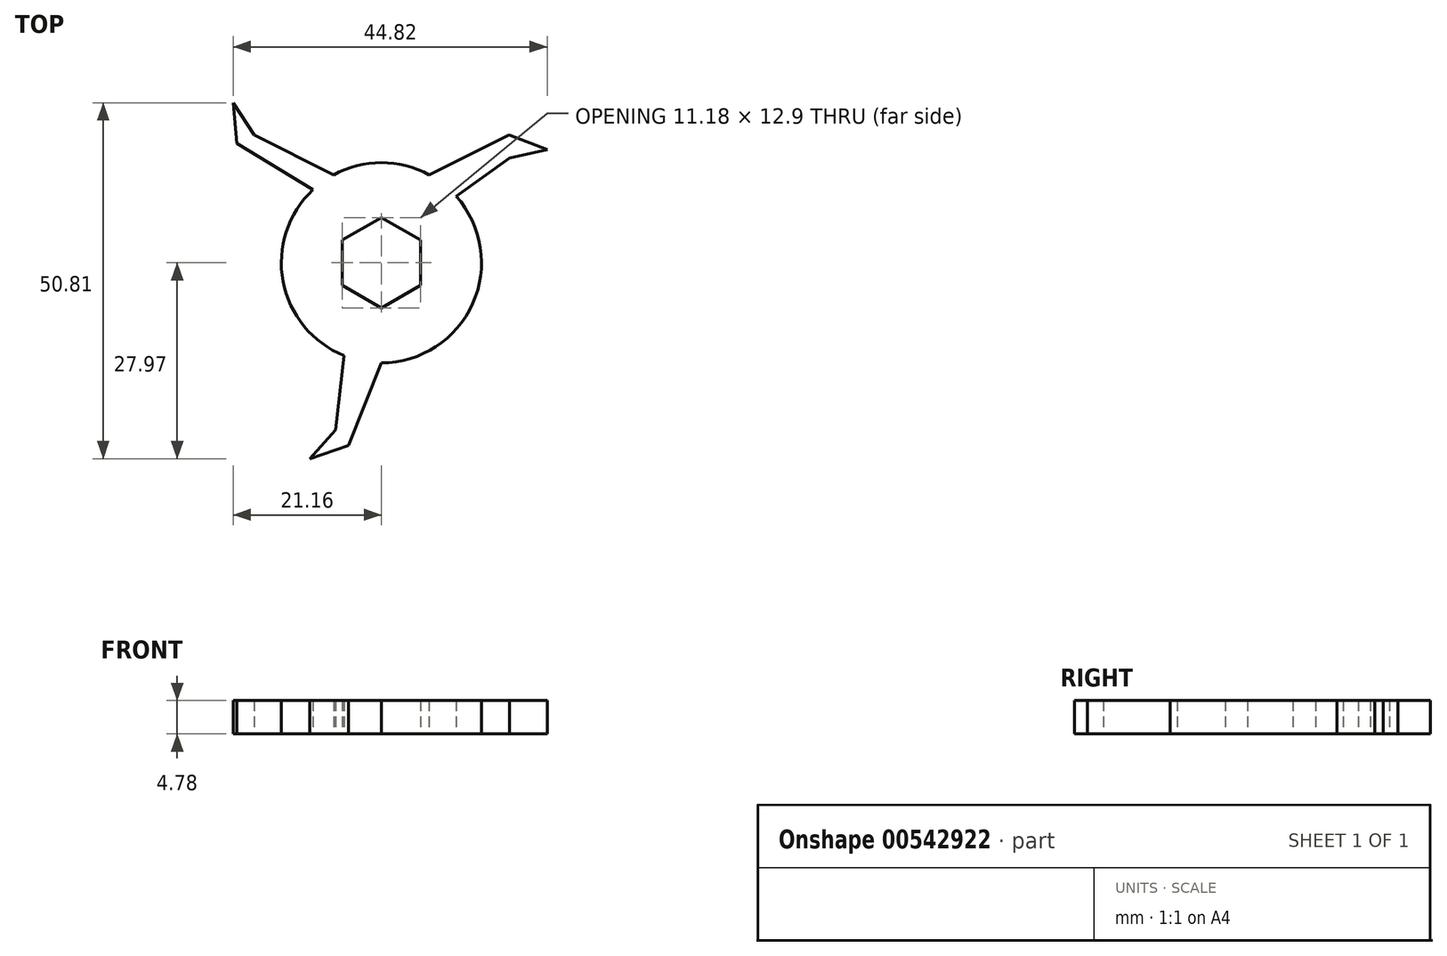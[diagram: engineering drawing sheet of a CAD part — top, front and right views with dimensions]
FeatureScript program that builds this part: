
annotation { "Feature Type Name" : "Feature", "Feature Type Description" : "" }
export const myFeature = defineFeature(function(context is Context, id is Id, definition is map)
    precondition{}
    {
        {
            var Q0;
            Q0=qCreatedBy(makeId("Top.planeOp"),FACE);
            var sketch = newSketch(context, id + "F0", { "sketchPlane" : qUnion([Q0])});
            skCircle(sketch, "E0", {"center": v(0, 0) * mm, "radius": 14.29 * mm});
            skPoint(sketch, "E1.end.orphan", {"position": v(12.7, 14.29) * mm});
            skPoint(sketch, "E1.start.orphan", {"position": v(0, 14.29) * mm});
            skPoint(sketch, "E2.start.orphan", {"position": v(13.26, 14.29) * mm});
            skPoint(sketch, "E3.start.orphan", {"position": v(12.7, 11.87) * mm});
            skPoint(sketch, "E4.end.orphan", {"position": v(-8.69, -11.34) * mm});
            skPoint(sketch, "E5.end.orphan", {"position": v(-17.74, -11.34) * mm});
            skPoint(sketch, "E6.start.orphan", {"position": v(0, -14.29) * mm});
            skLineSegment(sketch, "E7", {"start": v(0, -14.29) * mm, "end": v(-4.7, -26.09) * mm});
            skLineSegment(sketch, "E8", {"start": v(-4.7, -26.09) * mm, "end": v(-10.22, -27.97) * mm});
            skLineSegment(sketch, "E9", {"start": v(-10.22, -27.97) * mm, "end": v(-6.56, -23.85) * mm});
            skLineSegment(sketch, "E10", {"start": v(-6.56, -23.85) * mm, "end": v(-5.32, -13.26) * mm});
            skPoint(sketch, "E11.end.orphan", {"position": v(-9.8, 10.4) * mm});
            skPoint(sketch, "E12.end.orphan", {"position": v(-17.06, 10.4) * mm});
            skLineSegment(sketch, "E13", {"start": v(-9.8, 10.4) * mm, "end": v(-20.63, 17.02) * mm});
            skLineSegment(sketch, "E14", {"start": v(-20.63, 17.02) * mm, "end": v(-21.16, 22.84) * mm});
            skLineSegment(sketch, "E15", {"start": v(-21.16, 22.84) * mm, "end": v(-18.16, 18.21) * mm});
            skLineSegment(sketch, "E16", {"start": v(-18.16, 18.21) * mm, "end": v(-6.82, 12.55) * mm});
            skPoint(sketch, "E17.start.orphan", {"position": v(12.03, 11.87) * mm});
            skLineSegment(sketch, "E18", {"start": v(6.82, 12.55) * mm, "end": v(18.2, 18.21) * mm});
            skLineSegment(sketch, "E19", {"start": v(18.2, 18.21) * mm, "end": v(23.66, 16.14) * mm});
            skLineSegment(sketch, "E20", {"start": v(23.66, 16.14) * mm, "end": v(18.28, 14.93) * mm});
            skLineSegment(sketch, "E21", {"start": v(18.28, 14.93) * mm, "end": v(10.67, 9.5) * mm});
            skCircle(sketch, "E22.cCircle", {"center": v(0, 0) * mm, "radius": 5.59 * mm, "construction": true});
            skLineSegment(sketch, "E22.0", {"start": v(5.59, 3.23) * mm, "end": v(5.59, -3.23) * mm});
            skLineSegment(sketch, "E22.1", {"start": v(5.59, -3.23) * mm, "end": v(0, -6.45) * mm});
            skLineSegment(sketch, "E22.2", {"start": v(0, -6.45) * mm, "end": v(-5.59, -3.23) * mm});
            skLineSegment(sketch, "E22.3", {"start": v(-5.59, -3.23) * mm, "end": v(-5.59, 3.23) * mm});
            skLineSegment(sketch, "E22.4", {"start": v(-5.59, 3.23) * mm, "end": v(0, 6.45) * mm});
            skLineSegment(sketch, "E22.5", {"start": v(0, 6.45) * mm, "end": v(5.59, 3.23) * mm});
            skPoint(sketch, "E22.0.midPoint", {"position": v(5.59, 0) * mm});
            skSolve(sketch);
        }
        {
            var Q0;
            Q0 = qSketchRegion(id + "F0", true);
            extrude(context, id + "F1", {"entities" : qUnion([Q0]), "depth" : 4.78 * mm, "offsetDistance" : 25.4 * mm});
        }
    });
